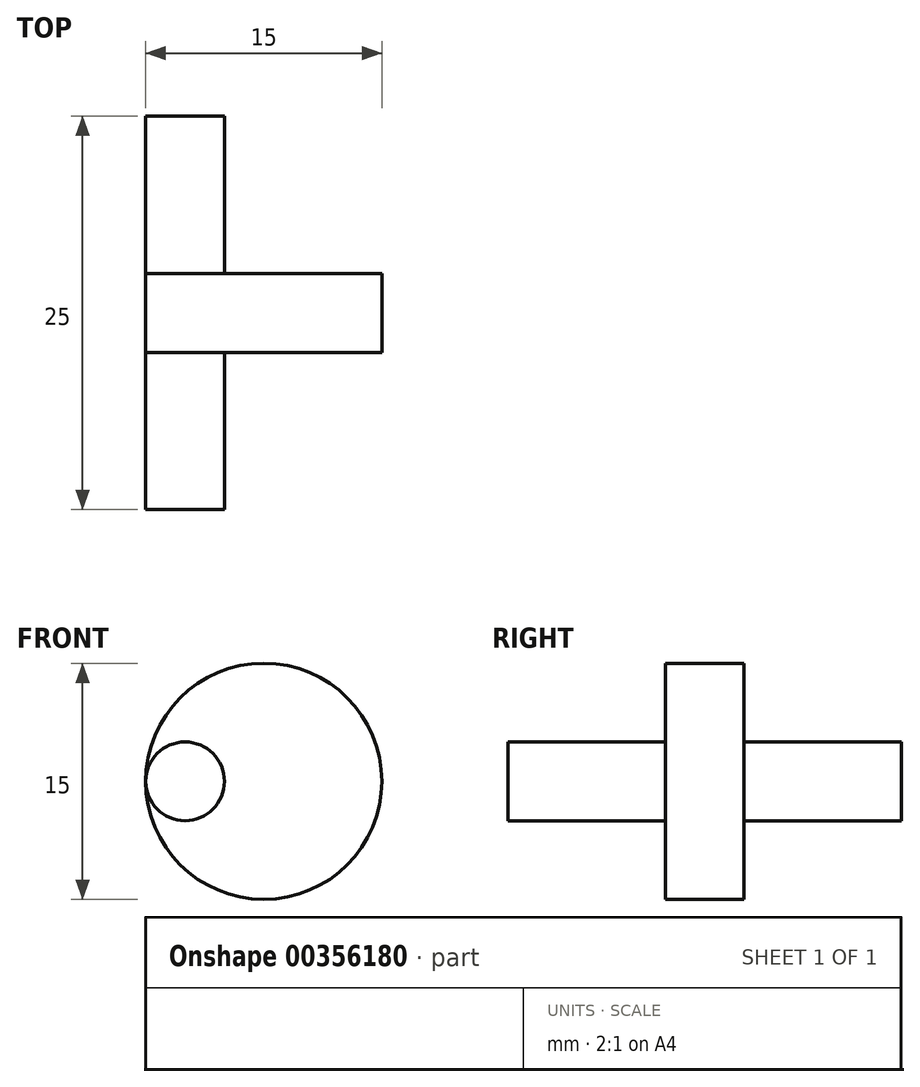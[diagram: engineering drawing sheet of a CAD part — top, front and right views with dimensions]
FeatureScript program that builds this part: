
annotation { "Feature Type Name" : "Feature", "Feature Type Description" : "" }
export const myFeature = defineFeature(function(context is Context, id is Id, definition is map)
    precondition{}
    {
        {
            var Q0;
            Q0=qCreatedBy(makeId("Front.planeOp"),FACE);
            var sketch = newSketch(context, id + "F0", { "sketchPlane" : qUnion([Q0])});
            skCircle(sketch, "E0", {"center": v(0, 0) * mm, "radius": 2.5 * mm});
            skCircle(sketch, "E1", {"center": v(5, 0) * mm, "radius": 7.5 * mm});
            skPoint(sketch, "E2", {"position": v(-2.5, 0) * mm});
            skSolve(sketch);
        }
        {
            var Q0;
            Q0=makeQuery(id+"F0.imprint","IMPRINT",FACE,{"disambiguationData":[TD([[makeQuery(id+"F0.imprint","IMPRINT",EDGE,{"derivedFrom":sQuery(id+"F0.wireOp",EDGE,"E0")}),1.0]])]});
            extrude(context, id + "F1", {"entities" : qUnion([Q0]), "endBound" : BoundingType.SYMMETRIC, "depth" : 25 * mm});
        }
        {
            var Q0;
            Q0 = qSketchRegion(id + "F0", true);
            extrude(context, id + "F2", {"entities" : qUnion([Q0]), "operationType" : NewBodyOperationType.ADD, "endBound" : BoundingType.SYMMETRIC, "depth" : 5 * mm});
        }
    });
